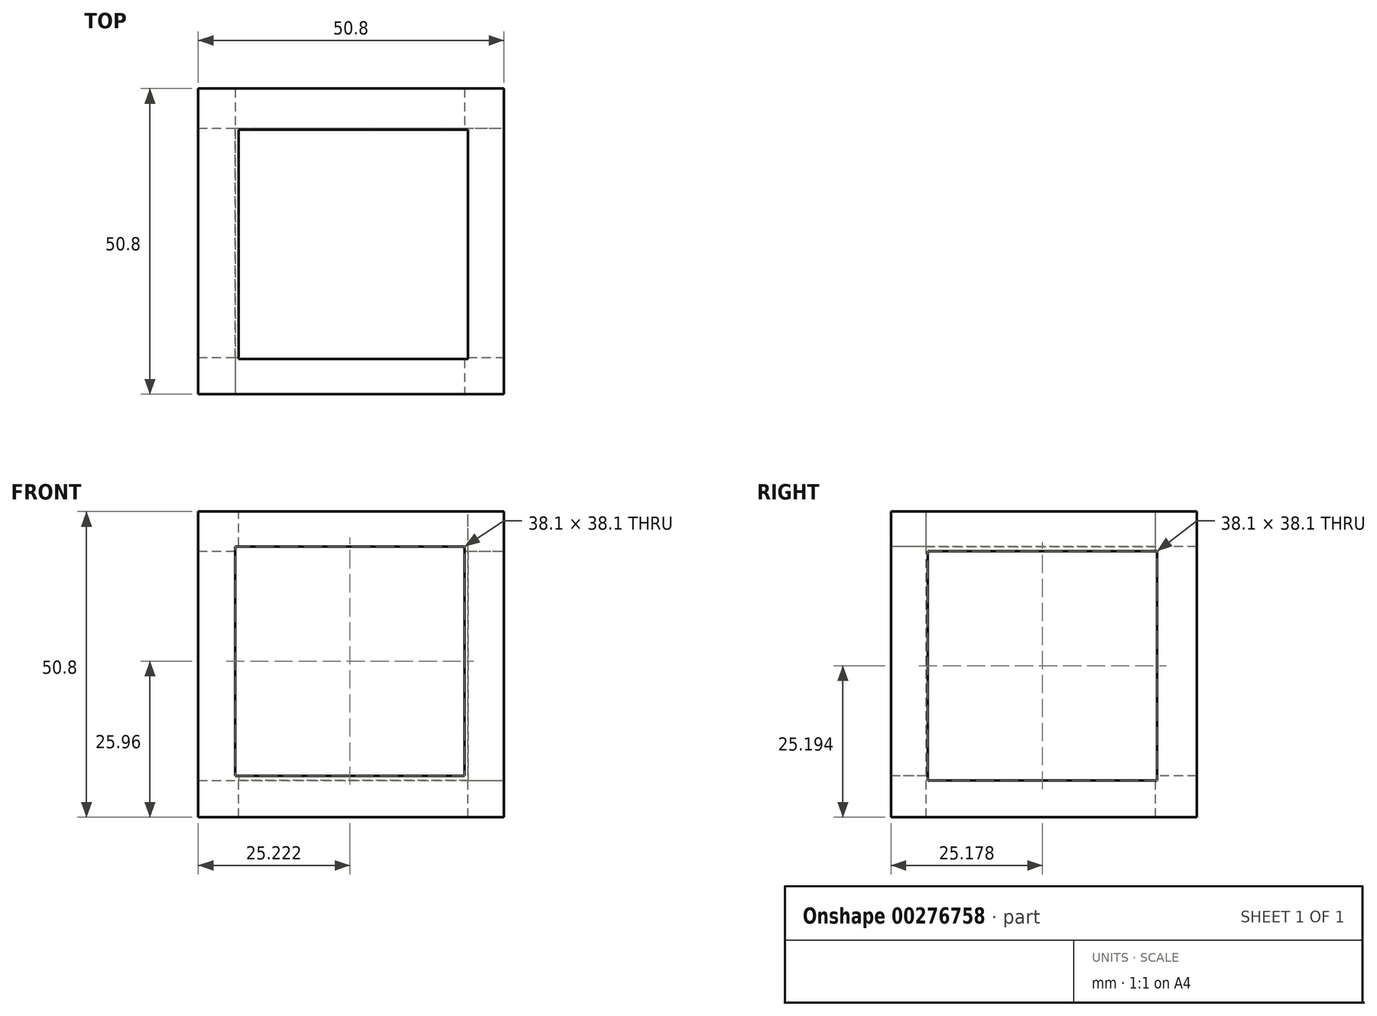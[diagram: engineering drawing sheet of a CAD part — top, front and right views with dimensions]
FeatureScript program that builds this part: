
annotation { "Feature Type Name" : "Feature", "Feature Type Description" : "" }
export const myFeature = defineFeature(function(context is Context, id is Id, definition is map)
    precondition{}
    {
        {
            var Q0;
            Q0=qCreatedBy(makeId("Right.planeOp"),FACE);
            var sketch = newSketch(context, id + "F0", { "sketchPlane" : qUnion([Q0])});
            skLineSegment(sketch, "E0.bottom", {"start": v(0, 0) * mm, "end": v(-50.8, 0) * mm});
            skLineSegment(sketch, "E0.top", {"start": v(0, -50.8) * mm, "end": v(-50.8, -50.8) * mm});
            skLineSegment(sketch, "E0.left", {"start": v(0, 0) * mm, "end": v(0, -50.8) * mm});
            skLineSegment(sketch, "E0.right", {"start": v(-50.8, 0) * mm, "end": v(-50.8, -50.8) * mm});
            skSolve(sketch);
        }
        {
            var Q0;
            Q0=makeQuery(id+"F0.imprint","IMPRINT",FACE,{"disambiguationData":[TD([[makeQuery(id+"F0.imprint","IMPRINT",EDGE,{"derivedFrom":sQuery(id+"F0.wireOp",EDGE,"E0.bottom")}),1.0]])]});
            extrude(context, id + "F1", {"entities" : qUnion([Q0]), "depth" : 50.8 * mm});
        }
        {
            var Q0;
            Q0=makeQuery(id+"F1.opExtrude","CAP_FACE",FACE,{"disambiguationData":[OSD([sQuery(id+"F0.wireOp",EDGE,"E0.bottom"),sQuery(id+"F0.wireOp",EDGE,"E0.top"),sQuery(id+"F0.wireOp",EDGE,"E0.left"),sQuery(id+"F0.wireOp",EDGE,"E0.right")])],"isStart":false});
            var sketch = newSketch(context, id + "F2", { "sketchPlane" : qUnion([Q0])});
            skLineSegment(sketch, "E1.bottom", {"start": v(-44.67, -6.56) * mm, "end": v(-6.57, -6.56) * mm});
            skLineSegment(sketch, "E1.top", {"start": v(-44.67, -44.66) * mm, "end": v(-6.57, -44.66) * mm});
            skLineSegment(sketch, "E1.left", {"start": v(-44.67, -6.56) * mm, "end": v(-44.67, -44.66) * mm});
            skLineSegment(sketch, "E1.right", {"start": v(-6.57, -6.56) * mm, "end": v(-6.57, -44.66) * mm});
            skSolve(sketch);
        }
        {
            var Q0;
            Q0=makeQuery(id+"F2.imprint","IMPRINT",FACE,{"disambiguationData":[TD([[makeQuery(id+"F2.imprint","IMPRINT",EDGE,{"derivedFrom":sQuery(id+"F2.wireOp",EDGE,"E1.bottom")}),-1.0]])]});
            extrude(context, id + "F3", {"entities" : qUnion([Q0]), "operationType" : NewBodyOperationType.REMOVE, "oppositeDirection" : true, "depth" : 50.8 * mm});
        }
        {
            var Q0;
            Q0=makeQuery(id+"F1.opExtrude","SWEPT_FACE",FACE,{"disambiguationData":[OSD([sQuery(id+"F0.wireOp",EDGE,"E0.right")])]});
            var sketch = newSketch(context, id + "F4", { "sketchPlane" : qUnion([Q0])});
            skLineSegment(sketch, "E2.bottom", {"start": v(6.17, -5.8) * mm, "end": v(44.27, -5.8) * mm});
            skLineSegment(sketch, "E2.top", {"start": v(6.17, -43.9) * mm, "end": v(44.27, -43.9) * mm});
            skLineSegment(sketch, "E2.left", {"start": v(6.17, -5.8) * mm, "end": v(6.17, -43.9) * mm});
            skLineSegment(sketch, "E2.right", {"start": v(44.27, -5.8) * mm, "end": v(44.27, -43.9) * mm});
            skSolve(sketch);
        }
        {
            var Q0;
            Q0=makeQuery(id+"F4.imprint","IMPRINT",FACE,{"disambiguationData":[TD([[makeQuery(id+"F4.imprint","IMPRINT",EDGE,{"derivedFrom":sQuery(id+"F4.wireOp",EDGE,"E2.bottom")}),-1.0]])]});
            extrude(context, id + "F5", {"entities" : qUnion([Q0]), "operationType" : NewBodyOperationType.REMOVE, "oppositeDirection" : true, "depth" : 50.8 * mm});
        }
        {
            var Q0;
            Q0=makeQuery(id+"F1.opExtrude","SWEPT_FACE",FACE,{"disambiguationData":[OSD([sQuery(id+"F0.wireOp",EDGE,"E0.bottom")])]});
            var sketch = newSketch(context, id + "F6", { "sketchPlane" : qUnion([Q0])});
            skLineSegment(sketch, "E3.bottom", {"start": v(6.73, -6.86) * mm, "end": v(44.83, -6.86) * mm});
            skLineSegment(sketch, "E3.top", {"start": v(6.73, -44.96) * mm, "end": v(44.83, -44.96) * mm});
            skLineSegment(sketch, "E3.left", {"start": v(6.73, -6.86) * mm, "end": v(6.73, -44.96) * mm});
            skLineSegment(sketch, "E3.right", {"start": v(44.83, -6.86) * mm, "end": v(44.83, -44.96) * mm});
            skSolve(sketch);
        }
        {
            var Q0;
            Q0=makeQuery(id+"F6.imprint","IMPRINT",FACE,{"disambiguationData":[TD([[makeQuery(id+"F6.imprint","IMPRINT",EDGE,{"derivedFrom":sQuery(id+"F6.wireOp",EDGE,"E3.bottom")}),-1.0]])]});
            extrude(context, id + "F7", {"entities" : qUnion([Q0]), "operationType" : NewBodyOperationType.REMOVE, "oppositeDirection" : true, "depth" : 50.8 * mm});
        }
    });
